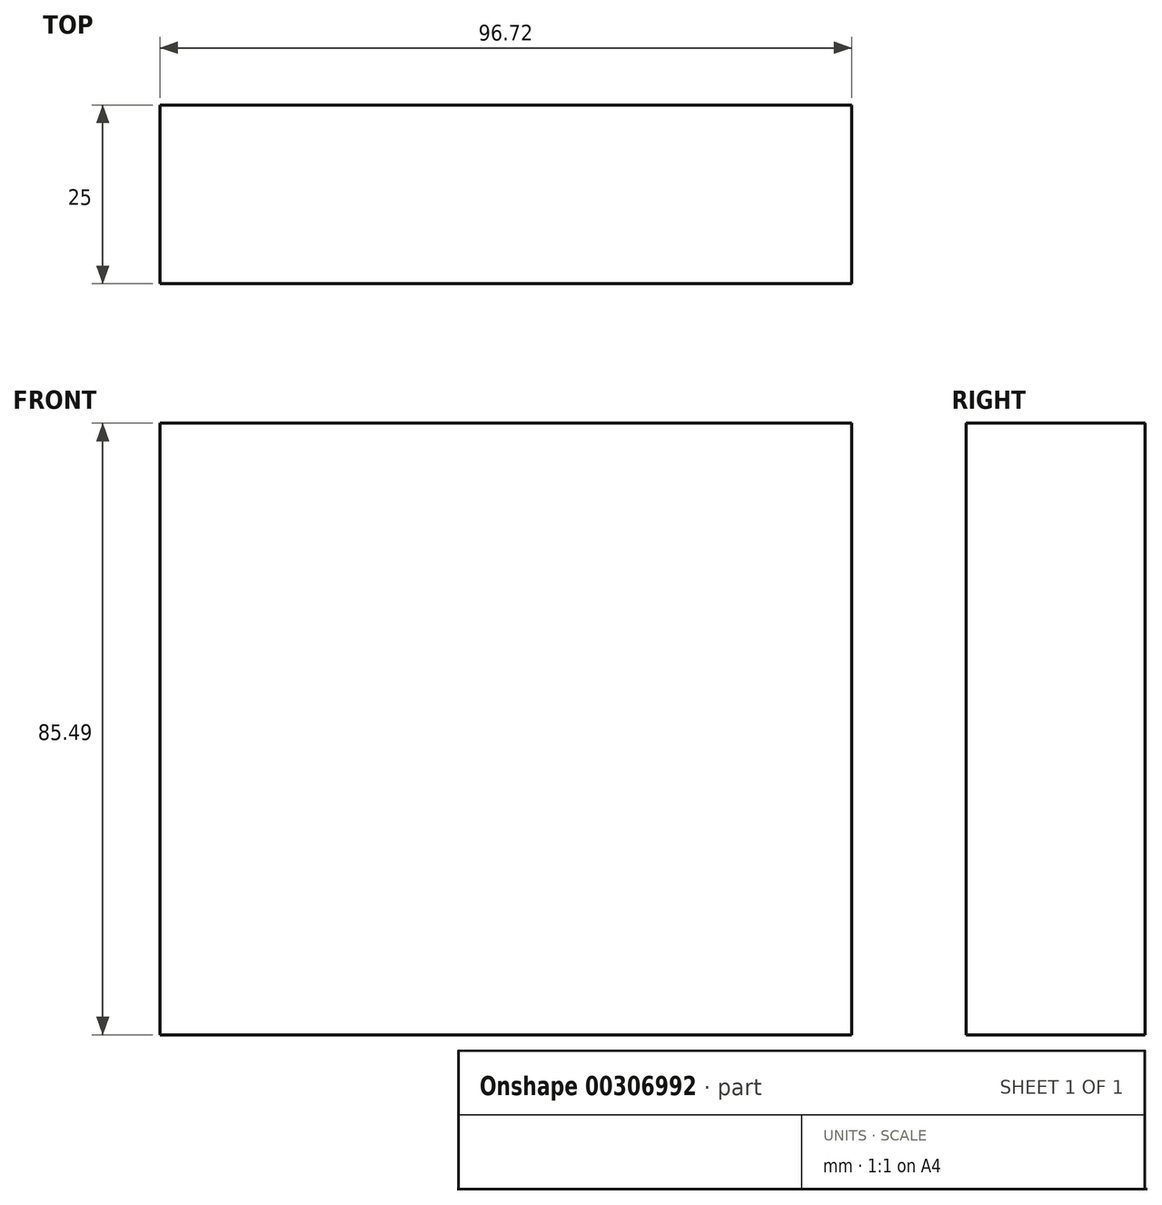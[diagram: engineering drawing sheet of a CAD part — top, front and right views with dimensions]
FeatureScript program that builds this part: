
annotation { "Feature Type Name" : "Feature", "Feature Type Description" : "" }
export const myFeature = defineFeature(function(context is Context, id is Id, definition is map)
    precondition{}
    {
        {
            var Q0;
            Q0=qCreatedBy(makeId("Front.planeOp"),FACE);
            var sketch = newSketch(context, id + "F0", { "sketchPlane" : qUnion([Q0])});
            skLineSegment(sketch, "E0.bottom", {"start": v(-97.04, 0) * mm, "end": v(-0.32, 0) * mm});
            skLineSegment(sketch, "E0.top", {"start": v(-97.04, 85.49) * mm, "end": v(-0.32, 85.49) * mm});
            skLineSegment(sketch, "E0.left", {"start": v(-97.04, 0) * mm, "end": v(-97.04, 85.49) * mm});
            skLineSegment(sketch, "E0.right", {"start": v(-0.32, 0) * mm, "end": v(-0.32, 85.49) * mm});
            skPoint(sketch, "E0.middle", {"position": v(-48.68, 42.74) * mm});
            skSolve(sketch);
        }
        {
            var Q0;
            Q0=makeQuery(id+"F0.imprint","IMPRINT",FACE,{"disambiguationData":[TD([[makeQuery(id+"F0.imprint","IMPRINT",EDGE,{"derivedFrom":sQuery(id+"F0.wireOp",EDGE,"E0.bottom")}),1.0]])]});
            extrude(context, id + "F1", {"entities" : qUnion([Q0]), "depth" : 25 * mm});
        }
    });
